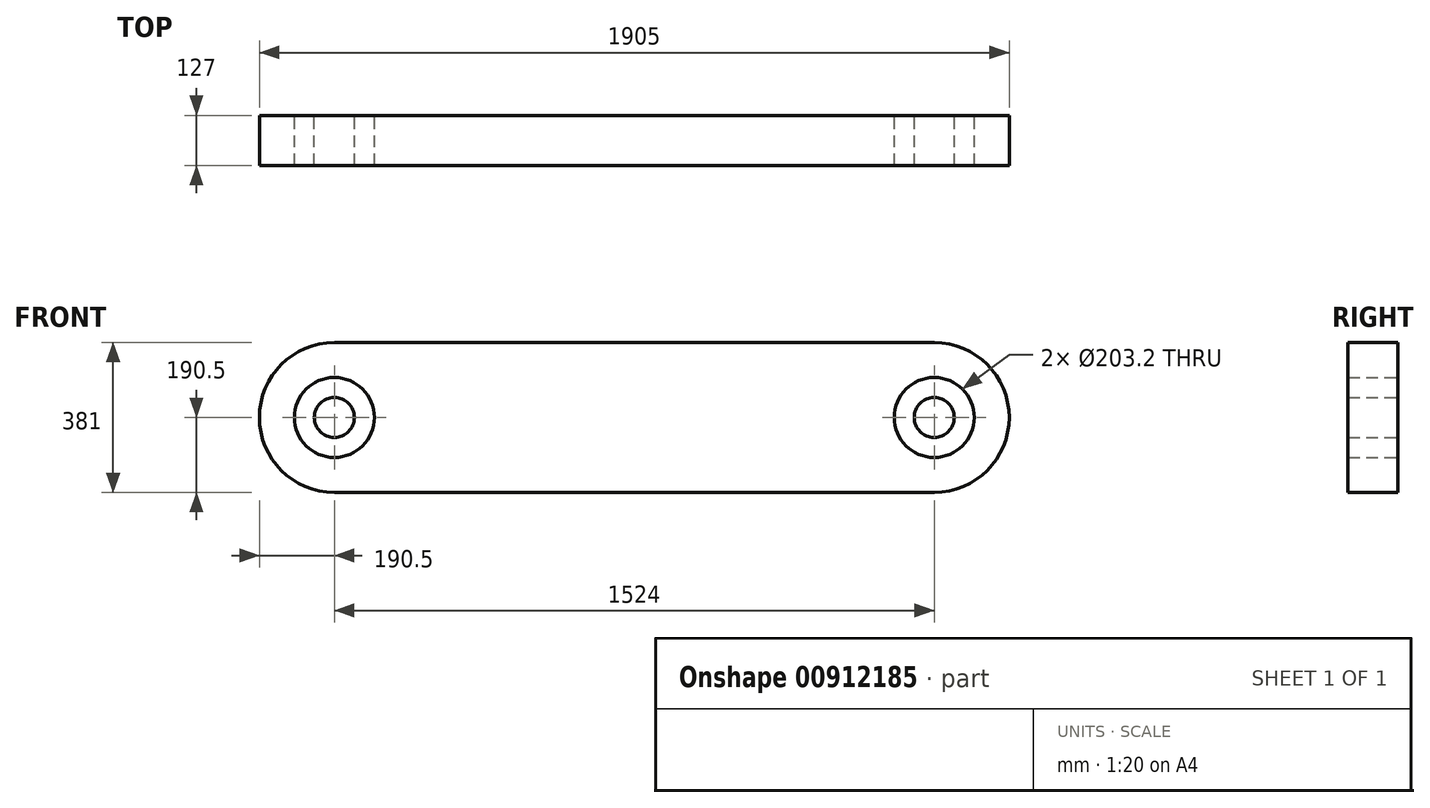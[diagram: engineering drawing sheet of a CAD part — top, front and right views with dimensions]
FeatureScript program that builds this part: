
annotation { "Feature Type Name" : "Feature", "Feature Type Description" : "" }
export const myFeature = defineFeature(function(context is Context, id is Id, definition is map)
    precondition{}
    {
        {
            var Q0;
            Q0=qCreatedBy(makeId("Front.planeOp"),FACE);
            var sketch = newSketch(context, id + "F0", { "sketchPlane" : qUnion([Q0])});
            skLineSegment(sketch, "E0.bottom", {"start": v(0, 0) * mm, "end": v(1524, 0) * mm});
            skLineSegment(sketch, "E0.top", {"start": v(0, 381) * mm, "end": v(1524, 381) * mm});
            skArc(sketch, "E1", {"start": v(0, 381) * mm, "mid": v(-190.5, 190.5) * mm, "end": v(0, 0) * mm});
            skCircle(sketch, "E2", {"center": v(0, 190.5) * mm, "radius": 101.6 * mm});
            skCircle(sketch, "E3", {"center": v(0, 190.5) * mm, "radius": 50.8 * mm});
            skArc(sketch, "E4", {"start": v(1524, 0) * mm, "mid": v(1714.5, 190.5) * mm, "end": v(1524, 381) * mm});
            skCircle(sketch, "E5", {"center": v(1524, 190.5) * mm, "radius": 101.6 * mm});
            skCircle(sketch, "E6", {"center": v(1524, 190.5) * mm, "radius": 50.8 * mm});
            skSolve(sketch);
        }
        {
            var Q0;
            Q0 = qSketchRegion(id + "F0", true);
            var Q1;
            Q1=makeQuery(id+"F0.imprint","IMPRINT",FACE,{"disambiguationData":[TD([[makeQuery(id+"F0.imprint","IMPRINT",EDGE,{"derivedFrom":sQuery(id+"F0.wireOp",EDGE,"E3")}),1.0]])]});
            var Q2;
            Q2=makeQuery(id+"F0.imprint","IMPRINT",FACE,{"disambiguationData":[TD([[makeQuery(id+"F0.imprint","IMPRINT",EDGE,{"derivedFrom":sQuery(id+"F0.wireOp",EDGE,"E6")}),1.0]])]});
            extrude(context, id + "F1", {"entities" : qUnion([Q0, Q1, Q2]), "depth" : 127 * mm, "offsetDistance" : 25.4 * mm});
        }
    });
